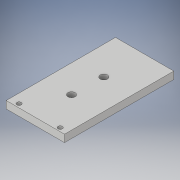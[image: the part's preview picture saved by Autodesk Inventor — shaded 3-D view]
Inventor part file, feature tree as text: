
AUTODESK INVENTOR PART (.ipt)
format: ipt  version: 2019.4 (Build 234330000, 330)  size: 102,400 bytes
history: native  units: in
note: dims shown in document units (in); Inventor stores cm internally (conversion verified against a paired STEP export)
features: sketch x3, hole x2, extrude x1
ambient origin geometry x8: Origin, YZ Plane, XZ Plane, XY Plane, X Axis, Y Axis, Z Axis, Center Point
bodies: Solid1 (feature_tree)
feature tree (6):
  extrude  "Extrusion1"  Depth=5.9055in
  hole  "Hole1"  [1 undecoded]
  hole  "Hole2"  [1 undecoded]
  sketch  "Sketch1"  dims[d0=3.1496in d1=5.9055in]
  sketch  "Sketch2"  dims[d2=0.3937in d3=0.0in]
  sketch  "Sketch3"  dims[d4=0.2362in d5=0.75in d6=0.119in d7=0.25in d8=0.5635in d9=1.0in d10=0.8108in d11=0.3937in d12=0.75in d13=0.119in d14=0.25in d15=0.5635in d16=1.0in d17=0.8108in]
note: 2 required parameter values undecoded (feature->parameter linkage not recoverable at this tier; creation-order binding heuristic only, values carry confidence <= 0.55)
